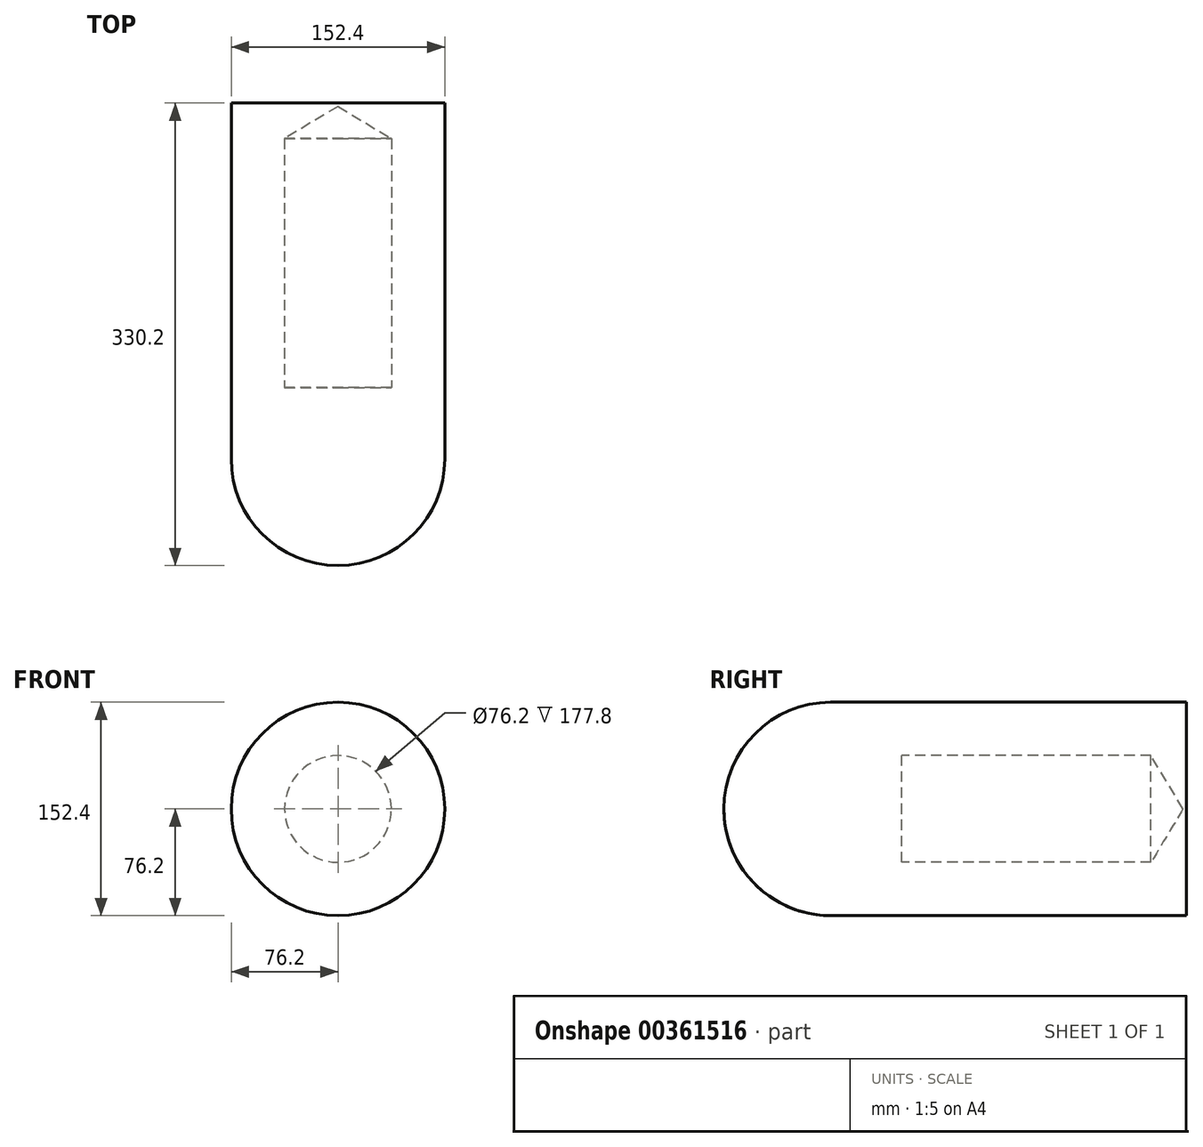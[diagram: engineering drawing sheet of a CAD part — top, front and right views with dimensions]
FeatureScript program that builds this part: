
annotation { "Feature Type Name" : "Feature", "Feature Type Description" : "" }
export const myFeature = defineFeature(function(context is Context, id is Id, definition is map)
    precondition{}
    {
        {
            var Q0;
            Q0=qCreatedBy(makeId("Front.planeOp"),FACE);
            var sketch = newSketch(context, id + "F0", { "sketchPlane" : qUnion([Q0])});
            skCircle(sketch, "E0", {"center": v(0, 0) * mm, "radius": 76.2 * mm});
            skSolve(sketch);
        }
        {
            var Q0;
            Q0=makeQuery(id+"F0.imprint","IMPRINT",FACE,{"disambiguationData":[TD([[makeQuery(id+"F0.imprint","IMPRINT",EDGE,{"derivedFrom":sQuery(id+"F0.wireOp",EDGE,"E0")}),1.0]])]});
            extrude(context, id + "F1", {"entities" : qUnion([Q0]), "oppositeDirection" : true, "depth" : 203.2 * mm});
        }
        {
            var Q0;
            Q0=makeQuery(id+"F1.opExtrude","CAP_FACE",FACE,{"disambiguationData":[OSD([sQuery(id+"F0.wireOp",EDGE,"E0")])],"isStart":true});
            var sketch = newSketch(context, id + "F2", { "sketchPlane" : qUnion([Q0])});
            skCircle(sketch, "E1", {"center": v(0, 0) * mm, "radius": 38.1 * mm});
            skSolve(sketch);
        }
        {
            var Q0;
            Q0=sQuery(id+"F2.wireOp",VERTEX,"E1.center");
            var Q1;
            Q1=makeQuery(id+"F1.opExtrude","SWEPT_BODY",BODY,{"disambiguationData":[OSD([sQuery(id+"F0.wireOp",EDGE,"E0")])]});
            hole(context, id + "F3", {"style" : HoleStyle.SIMPLE, "endStyle" : HoleEndStyle.BLIND, "holeDiameter" : 76.2 * mm, "holeDepth" : 177.8 * mm, "isTappedThrough" : true, "tappedDepth" : 12.7 * mm, "tapClearance" : 3, "startFromSketch" : true, "locations" : qUnion([Q0]), "scope" : qUnion([Q1])});
        }
        {
            var Q0;
            Q0=makeQuery(id+"F0.imprint","IMPRINT",FACE,{"disambiguationData":[TD([[makeQuery(id+"F0.imprint","IMPRINT",EDGE,{"derivedFrom":sQuery(id+"F0.wireOp",EDGE,"E0")}),1.0]])]});
            var Q1;
            Q1=makeQuery(id+"F2.imprint","IMPRINT",FACE,{"disambiguationData":[TD([[makeQuery(id+"F2.imprint","IMPRINT",EDGE,{"derivedFrom":sQuery(id+"F2.wireOp",EDGE,"E1")}),1.0]])]});
            extrude(context, id + "F4", {"entities" : qUnion([Q0, Q1]), "operationType" : NewBodyOperationType.ADD, "depth" : 25.4 * mm});
        }
        {
            var Q0;
            Q0=makeQuery(id+"F4.opExtrude","CAP_FACE",FACE,{"disambiguationData":[OSD([sQuery(id+"F0.wireOp",EDGE,"E0")])],"isStart":false});
            extrude(context, id + "F5", {"entities" : qUnion([Q0]), "operationType" : NewBodyOperationType.ADD, "depth" : 101.6 * mm});
        }
        {
            var Q0;
            Q0=makeQuery(id+"F5.opExtrude","CAP_EDGE",EDGE,{"disambiguationData":[OSD([sQuery(id+"F0.wireOp",EDGE,"E0")])],"isStart":false});
            fillet(context, id + "F6", {"entities" : qUnion([Q0]), "radius" : 76.2 * mm, "tangentPropagation" : true, "allowEdgeOverflow" : false});
        }
    });
